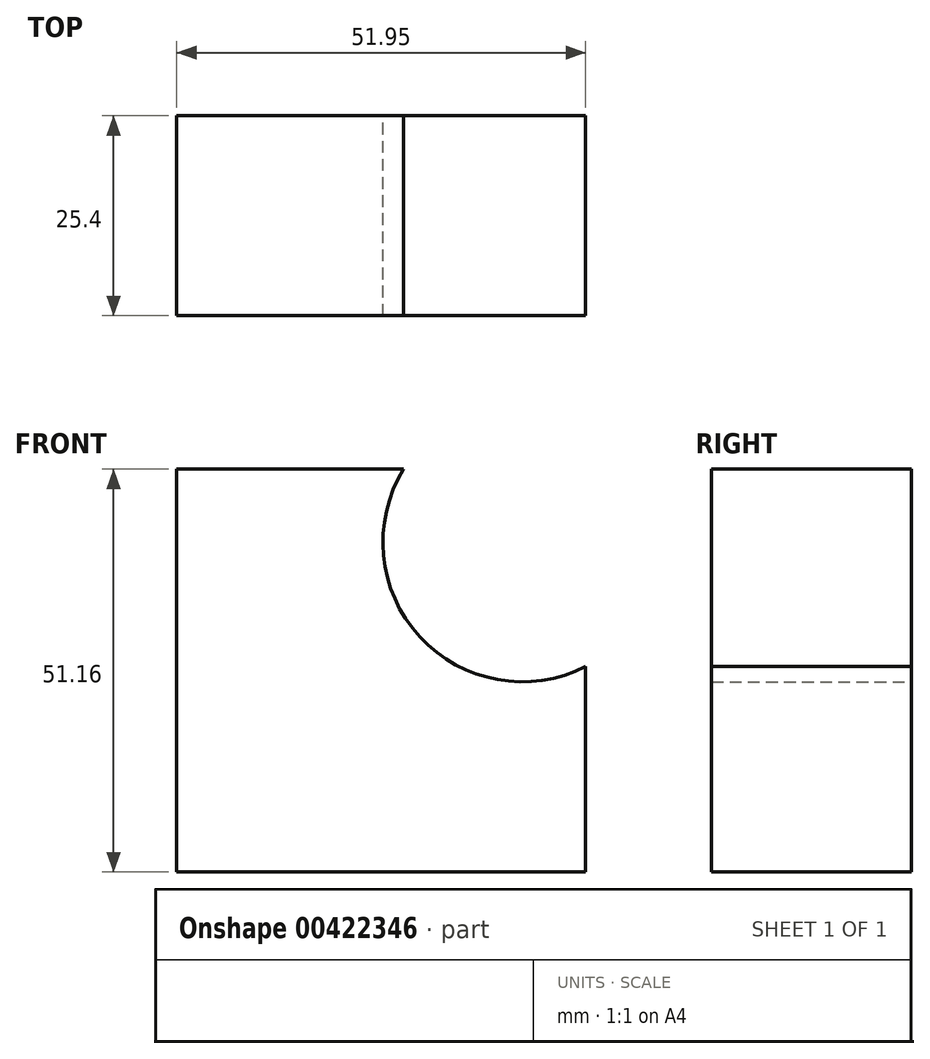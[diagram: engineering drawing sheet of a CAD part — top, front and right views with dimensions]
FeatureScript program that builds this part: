
annotation { "Feature Type Name" : "Feature", "Feature Type Description" : "" }
export const myFeature = defineFeature(function(context is Context, id is Id, definition is map)
    precondition{}
    {
        {
            var Q0;
            Q0=qCreatedBy(makeId("Front.planeOp"),FACE);
            var sketch = newSketch(context, id + "F0", { "sketchPlane" : qUnion([Q0])});
            skLineSegment(sketch, "E0", {"start": v(-23.9, 40.1) * mm, "end": v(-23.9, -11.06) * mm});
            skLineSegment(sketch, "E1", {"start": v(-23.9, -11.06) * mm, "end": v(28.05, -11.06) * mm});
            skLineSegment(sketch, "E2", {"start": v(28.05, -11.06) * mm, "end": v(28.05, 15.01) * mm});
            skLineSegment(sketch, "E3", {"start": v(-23.9, 40.1) * mm, "end": v(4.94, 40.1) * mm});
            skArc(sketch, "E4", {"start": v(4.94, 40.1) * mm, "mid": v(6.98, 18.8) * mm, "end": v(28.05, 15.01) * mm});
            skSolve(sketch);
        }
        {
            var Q0;
            Q0 = qSketchRegion(id + "F0", true);
            extrude(context, id + "F1", {"entities" : qUnion([Q0]), "depth" : 25.4 * mm});
        }
    });
